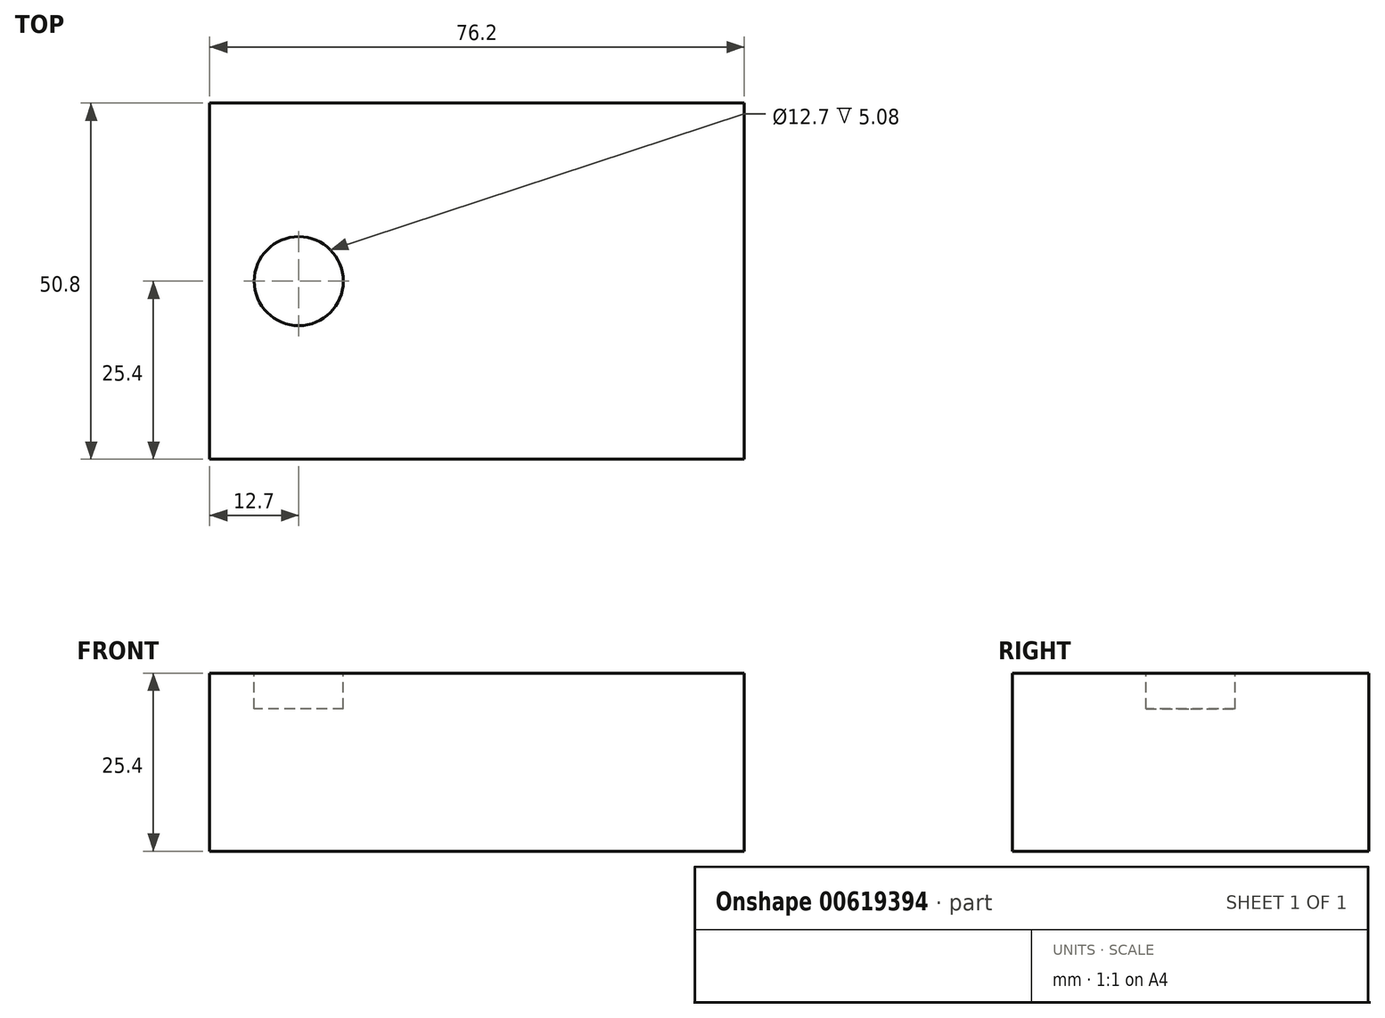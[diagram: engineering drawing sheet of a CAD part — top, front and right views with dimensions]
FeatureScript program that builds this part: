
annotation { "Feature Type Name" : "Feature", "Feature Type Description" : "" }
export const myFeature = defineFeature(function(context is Context, id is Id, definition is map)
    precondition{}
    {
        {
            var Q0;
            Q0=qCreatedBy(makeId("Front.planeOp"),FACE);
            var sketch = newSketch(context, id + "F0", { "sketchPlane" : qUnion([Q0])});
            skLineSegment(sketch, "E0.bottom", {"start": v(0, 0) * mm, "end": v(76.2, 0) * mm});
            skLineSegment(sketch, "E0.top", {"start": v(0, 25.4) * mm, "end": v(76.2, 25.4) * mm});
            skLineSegment(sketch, "E0.left", {"start": v(0, 0) * mm, "end": v(0, 25.4) * mm});
            skLineSegment(sketch, "E0.right", {"start": v(76.2, 0) * mm, "end": v(76.2, 25.4) * mm});
            skSolve(sketch);
        }
        {
            var Q0;
            Q0=makeQuery(id+"F0.imprint","IMPRINT",FACE,{"disambiguationData":[TD([[makeQuery(id+"F0.imprint","IMPRINT",EDGE,{"derivedFrom":sQuery(id+"F0.wireOp",EDGE,"E0.bottom")}),1.0]])]});
            extrude(context, id + "F1", {"entities" : qUnion([Q0]), "endBound" : BoundingType.SYMMETRIC, "depth" : 50.8 * mm, "offsetDistance" : 25.4 * mm});
        }
        {
            var Q0;
            Q0=makeQuery(id+"F1.opExtrude","SWEPT_FACE",FACE,{"disambiguationData":[OSD([sQuery(id+"F0.wireOp",EDGE,"E0.top")])]});
            var sketch = newSketch(context, id + "F2", { "sketchPlane" : qUnion([Q0])});
            skCircle(sketch, "E1", {"center": v(12.7, 0) * mm, "radius": 6.35 * mm});
            skPoint(sketch, "E1.centerSnap0", {"position": v(0, 0) * mm});
            skSolve(sketch);
        }
        {
            var Q0;
            Q0=makeQuery(id+"F2.imprint","IMPRINT",FACE,{"disambiguationData":[TD([[makeQuery(id+"F2.imprint","IMPRINT",EDGE,{"derivedFrom":sQuery(id+"F2.wireOp",EDGE,"E1")}),1.0]])]});
            extrude(context, id + "F3", {"entities" : qUnion([Q0]), "operationType" : NewBodyOperationType.REMOVE, "oppositeDirection" : true, "depth" : 5.08 * mm, "offsetDistance" : 25.4 * mm});
        }
    });
